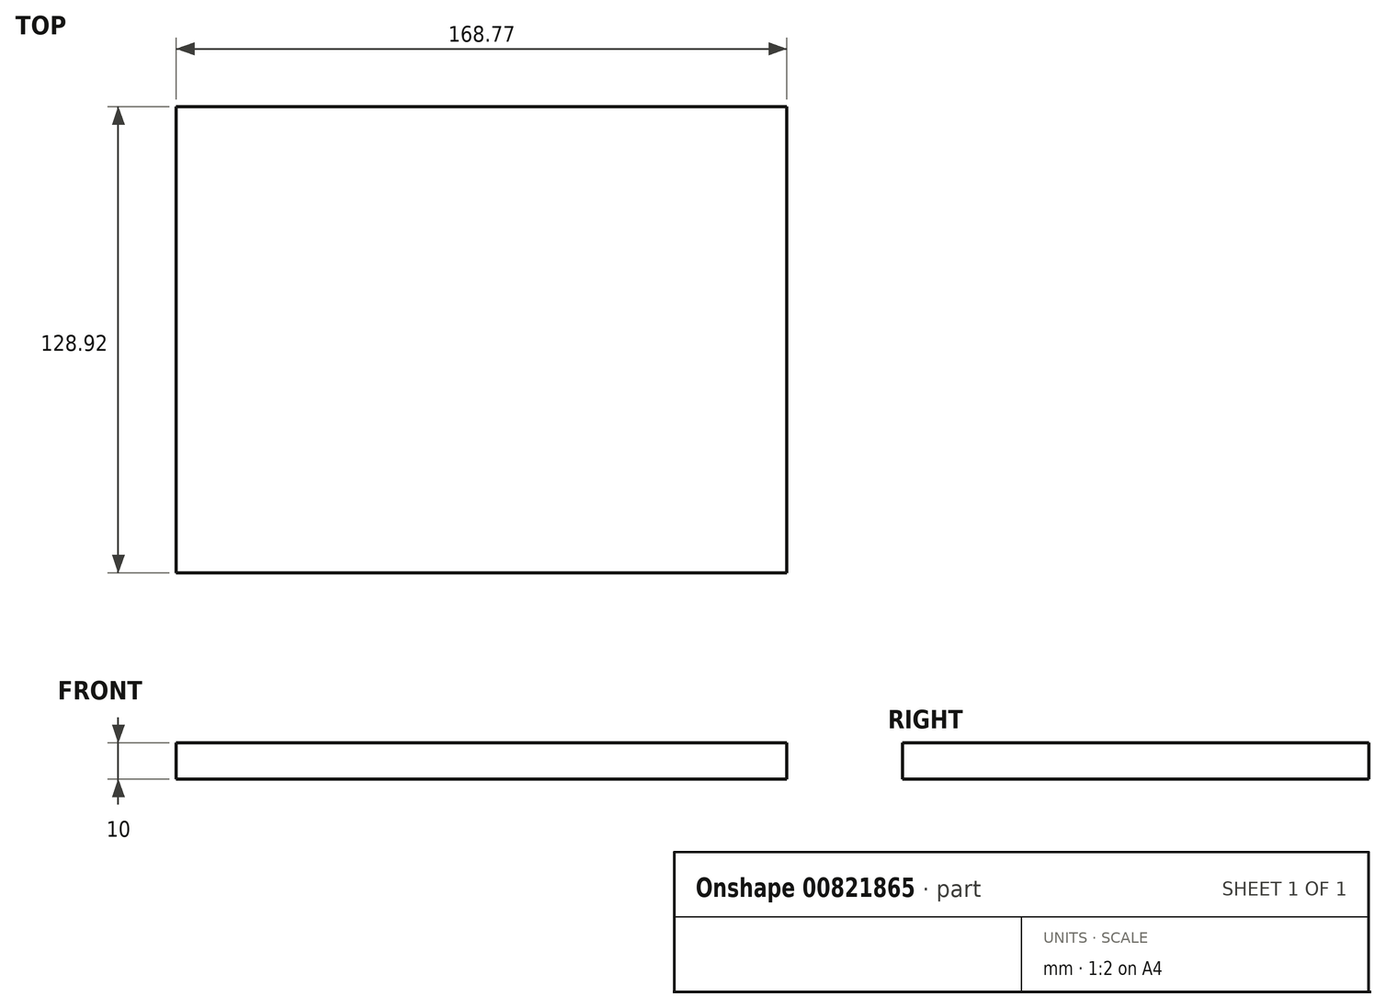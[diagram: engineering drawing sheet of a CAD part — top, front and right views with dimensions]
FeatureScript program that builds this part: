
annotation { "Feature Type Name" : "Feature", "Feature Type Description" : "" }
export const myFeature = defineFeature(function(context is Context, id is Id, definition is map)
    precondition{}
    {
        {
            var Q0;
            Q0=qCreatedBy(makeId("Top.planeOp"),FACE);
            var sketch = newSketch(context, id + "F0", { "sketchPlane" : qUnion([Q0])});
            skLineSegment(sketch, "E0.bottom", {"start": v(-108.05, 69) * mm, "end": v(60.72, 69) * mm});
            skLineSegment(sketch, "E0.top", {"start": v(-108.05, -59.9) * mm, "end": v(60.72, -59.9) * mm});
            skLineSegment(sketch, "E0.left", {"start": v(-108.05, 69) * mm, "end": v(-108.05, -59.9) * mm});
            skLineSegment(sketch, "E0.right", {"start": v(60.72, 69) * mm, "end": v(60.72, -59.9) * mm});
            skSolve(sketch);
        }
        {
            var Q0;
            Q0=makeQuery(id+"F0.imprint","IMPRINT",FACE,{"disambiguationData":[TD([[makeQuery(id+"F0.imprint","IMPRINT",EDGE,{"derivedFrom":sQuery(id+"F0.wireOp",EDGE,"E0.bottom")}),-1.0]])]});
            extrude(context, id + "F1", {"entities" : qUnion([Q0]), "endBound" : BoundingType.SYMMETRIC, "depth" : 10 * mm, "offsetDistance" : 25.4 * mm});
        }
    });
